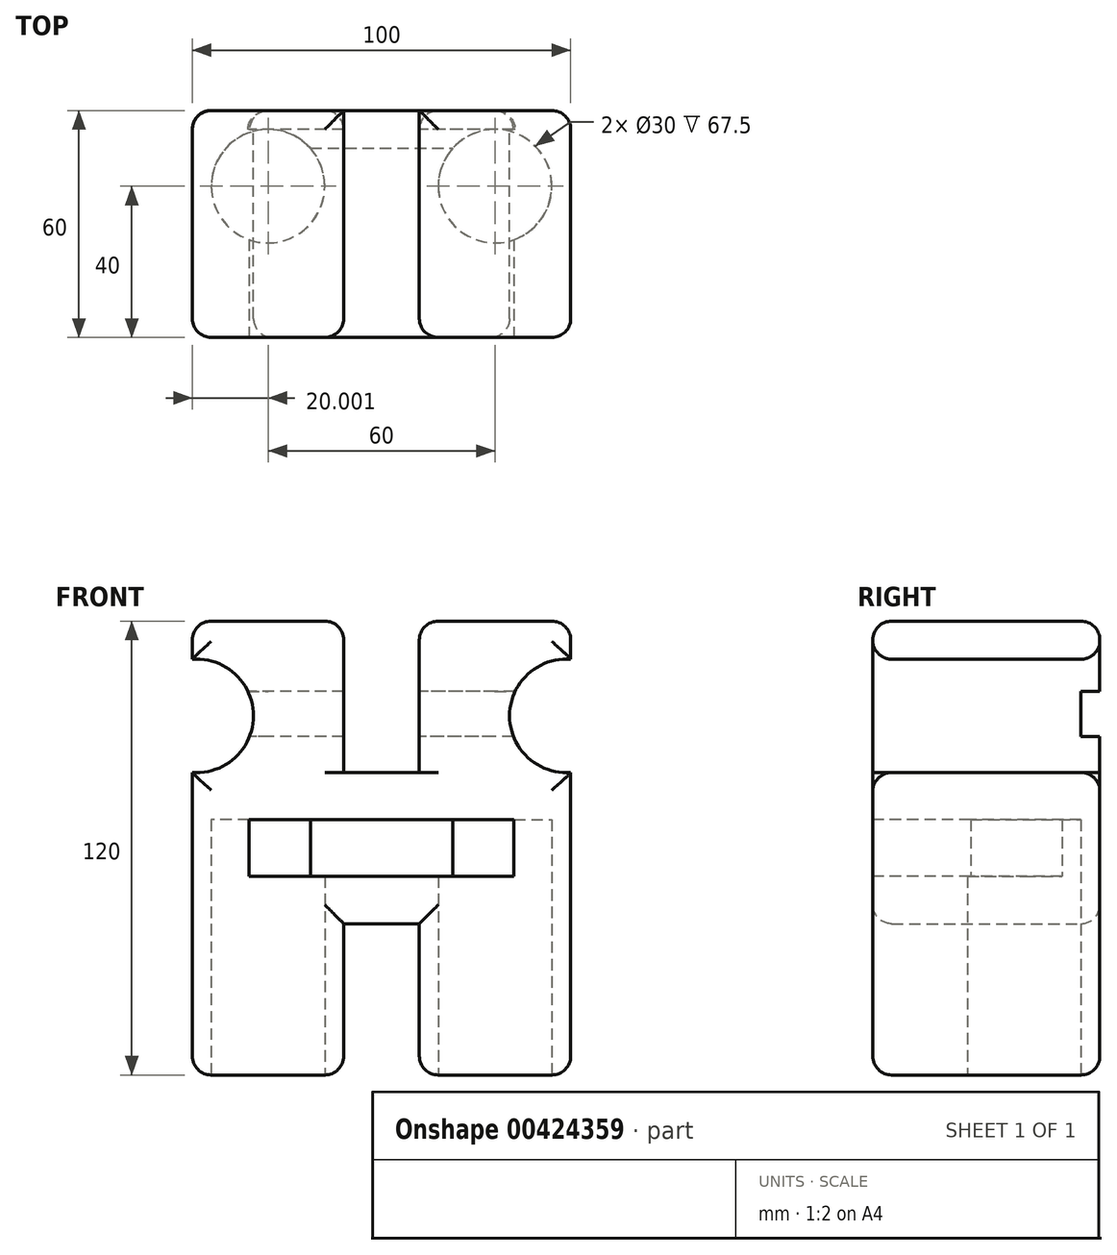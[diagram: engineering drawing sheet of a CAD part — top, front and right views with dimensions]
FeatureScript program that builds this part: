
annotation { "Feature Type Name" : "Feature", "Feature Type Description" : "" }
export const myFeature = defineFeature(function(context is Context, id is Id, definition is map)
    precondition{}
    {
        {
            var Q0;
            Q0=qCreatedBy(makeId("Front.planeOp"),FACE);
            var sketch = newSketch(context, id + "F0", { "sketchPlane" : qUnion([Q0])});
            skLineSegment(sketch, "E0.bottom", {"start": v(-48.04, 59.25) * mm, "end": v(-8.04, 59.25) * mm});
            skLineSegment(sketch, "E0.top", {"start": v(-48.04, -60.75) * mm, "end": v(-8.04, -60.75) * mm});
            skLineSegment(sketch, "E0.left", {"start": v(-48.04, 19.25) * mm, "end": v(-48.04, -60.75) * mm});
            skLineSegment(sketch, "E0.right", {"start": v(51.96, 19.25) * mm, "end": v(51.96, -60.75) * mm});
            skLineSegment(sketch, "E1", {"start": v(-8.04, 59.25) * mm, "end": v(-8.04, 19.25) * mm});
            skLineSegment(sketch, "E2", {"start": v(-8.04, 19.25) * mm, "end": v(11.96, 19.25) * mm});
            skLineSegment(sketch, "E3", {"start": v(11.96, 19.25) * mm, "end": v(11.96, 59.25) * mm});
            skLineSegment(sketch, "E4", {"start": v(11.96, -60.75) * mm, "end": v(11.96, -20.75) * mm});
            skLineSegment(sketch, "E5", {"start": v(11.96, -20.75) * mm, "end": v(-8.04, -20.75) * mm});
            skLineSegment(sketch, "E6", {"start": v(-8.04, -20.75) * mm, "end": v(-8.04, -60.75) * mm});
            skLineSegment(sketch, "E7.trimOffspring", {"start": v(11.96, -60.75) * mm, "end": v(51.96, -60.75) * mm});
            skLineSegment(sketch, "E8.trimOffspring", {"start": v(11.96, 59.25) * mm, "end": v(51.96, 59.25) * mm});
            skLineSegment(sketch, "E9", {"start": v(11.96, 19.25) * mm, "end": v(-8.04, 19.25) * mm});
            skLineSegment(sketch, "E10", {"start": v(-48.04, 59.25) * mm, "end": v(-48.04, 49.16) * mm});
            skLineSegment(sketch, "E11", {"start": v(51.96, 59.25) * mm, "end": v(51.96, 49.16) * mm});
            skArc(sketch, "E12", {"start": v(-48.04, 19.25) * mm, "mid": v(-31.88, 34.2) * mm, "end": v(-48.04, 49.16) * mm});
            skArc(sketch, "E13", {"start": v(51.96, 49.16) * mm, "mid": v(35.8, 34.2) * mm, "end": v(51.96, 19.25) * mm});
            skSolve(sketch);
        }
        {
            var Q0;
            Q0=makeQuery(id+"F0.imprint","IMPRINT",FACE,{"disambiguationData":[TD([[makeQuery(id+"F0.imprint","IMPRINT",EDGE,{"derivedFrom":sQuery(id+"F0.wireOp",EDGE,"E0.bottom")}),-1.0]])]});
            extrude(context, id + "F1", {"entities" : qUnion([Q0]), "depth" : 60 * mm});
        }
        {
            var Q0;
            Q0=makeQuery(id+"F1.opExtrude","CAP_FACE",FACE,{"disambiguationData":[OSD([sQuery(id+"F0.wireOp",EDGE,"E0.bottom"),sQuery(id+"F0.wireOp",EDGE,"E0.top"),sQuery(id+"F0.wireOp",EDGE,"E0.left"),sQuery(id+"F0.wireOp",EDGE,"E0.right"),sQuery(id+"F0.wireOp",EDGE,"E1"),sQuery(id+"F0.wireOp",EDGE,"E2"),sQuery(id+"F0.wireOp",EDGE,"E3"),sQuery(id+"F0.wireOp",EDGE,"E4"),sQuery(id+"F0.wireOp",EDGE,"E5"),sQuery(id+"F0.wireOp",EDGE,"E6"),sQuery(id+"F0.wireOp",EDGE,"E7.trimOffspring"),sQuery(id+"F0.wireOp",EDGE,"E8.trimOffspring")])],"isStart":false});
            var sketch = newSketch(context, id + "F2", { "sketchPlane" : qUnion([Q0])});
            skLineSegment(sketch, "E14.bottom", {"start": v(-33.04, 6.75) * mm, "end": v(36.96, 6.75) * mm});
            skLineSegment(sketch, "E14.top", {"start": v(-33.04, -8.25) * mm, "end": v(36.96, -8.25) * mm});
            skLineSegment(sketch, "E14.left", {"start": v(-33.04, 6.75) * mm, "end": v(-33.04, -8.25) * mm});
            skLineSegment(sketch, "E14.right", {"start": v(36.96, 6.75) * mm, "end": v(36.96, -8.25) * mm});
            skSolve(sketch);
        }
        {
            var Q0;
            Q0=makeQuery(id+"F2.imprint","IMPRINT",FACE,{"disambiguationData":[TD([[makeQuery(id+"F2.imprint","IMPRINT",EDGE,{"derivedFrom":sQuery(id+"F2.wireOp",EDGE,"E14.bottom")}),-1.0]])]});
            extrude(context, id + "F3", {"entities" : qUnion([Q0]), "operationType" : NewBodyOperationType.REMOVE, "oppositeDirection" : true, "depth" : 50 * mm});
        }
        {
            var Q0;
            Q0=makeQuery(id+"F1.opExtrude","SWEPT_FACE",FACE,{"disambiguationData":[OSD([sQuery(id+"F0.wireOp",EDGE,"E0.top")])]});
            var sketch = newSketch(context, id + "F4", { "sketchPlane" : qUnion([Q0])});
            skCircle(sketch, "E15", {"center": v(-28.04, 20) * mm, "radius": 15 * mm});
            skSolve(sketch);
        }
        {
            var Q0;
            Q0=makeQuery(id+"F1.opExtrude","SWEPT_FACE",FACE,{"disambiguationData":[OSD([sQuery(id+"F0.wireOp",EDGE,"E7.trimOffspring")])]});
            var sketch = newSketch(context, id + "F5", { "sketchPlane" : qUnion([Q0])});
            skCircle(sketch, "E16", {"center": v(31.96, 20) * mm, "radius": 15 * mm});
            skSolve(sketch);
        }
        {
            var Q0;
            Q0=makeQuery(id+"F4.imprint","IMPRINT",FACE,{"disambiguationData":[TD([[makeQuery(id+"F4.imprint","IMPRINT",EDGE,{"derivedFrom":sQuery(id+"F4.wireOp",EDGE,"E15")}),1.0]])]});
            var Q1;
            Q1=makeQuery(id+"F5.imprint","IMPRINT",FACE,{"disambiguationData":[TD([[makeQuery(id+"F5.imprint","IMPRINT",EDGE,{"derivedFrom":sQuery(id+"F5.wireOp",EDGE,"E16")}),1.0]])]});
            var Q2;
            Q2=sQuery(id+"F4.wireOp",EDGE,"E15");
            extrude(context, id + "F6", {"entities" : qUnion([Q0, Q1]), "operationType" : NewBodyOperationType.REMOVE, "surfaceEntities" : qUnion([Q2]), "oppositeDirection" : true, "depth" : 67.5 * mm});
        }
        {
            var Q0;
            Q0=makeQuery(id+"F0.imprint","IMPRINT",FACE,{"disambiguationData":[TD([[makeQuery(id+"F0.imprint","IMPRINT",EDGE,{"derivedFrom":sQuery(id+"F0.wireOp",EDGE,"E0.bottom")}),-1.0]])]});
            var sketch = newSketch(context, id + "F7", { "sketchPlane" : qUnion([Q0])});
            skLineSegment(sketch, "E17.bottom", {"start": v(38, 40.7) * mm, "end": v(-38.4, 40.7) * mm});
            skLineSegment(sketch, "E17.top", {"start": v(38, 28.7) * mm, "end": v(-38.4, 28.7) * mm});
            skLineSegment(sketch, "E17.left", {"start": v(38, 40.7) * mm, "end": v(38, 28.7) * mm});
            skLineSegment(sketch, "E17.right", {"start": v(-38.4, 40.7) * mm, "end": v(-38.4, 28.7) * mm});
            skSolve(sketch);
        }
        {
            var Q0;
            {var subQ0=sQuery(id+"F7.wireOp",EDGE,"E17.left");Q0=makeQuery(id+"F7.imprint","IMPRINT",FACE,{"disambiguationData":[TD([[makeQuery(id+"F7.imprint","IMPRINT",EDGE,{"derivedFrom":subQ0}),-1.0]])]});}
            var Q1;
            {var subQ0=sQuery(id+"F7.wireOp",EDGE,"E17.bottom");var subQ1=makeQuery(id+"F0.imprint","IMPRINT",EDGE,{"derivedFrom":sQuery(id+"F0.wireOp",EDGE,"E3")});var subQ2=makeQuery(id+"F7.imprint","INTERSECT",VERTEX,{"derivedFrom":[subQ1,subQ0]});Q1=makeQuery(id+"F7.imprint","IMPRINT",FACE,{"disambiguationData":[TD([[makeQuery(id+"F7.imprint","IMPRINT",EDGE,{"disambiguationData":[TD([[subQ2,-1.0]])],"derivedFrom":subQ0}),1.0]])]});}
            var Q2;
            {var subQ0=sQuery(id+"F7.wireOp",EDGE,"E17.bottom");var subQ1=makeQuery(id+"F0.imprint","IMPRINT",EDGE,{"derivedFrom":sQuery(id+"F0.wireOp",EDGE,"E1")});var subQ2=makeQuery(id+"F7.imprint","INTERSECT",VERTEX,{"derivedFrom":[subQ1,subQ0]});Q2=makeQuery(id+"F7.imprint","IMPRINT",FACE,{"disambiguationData":[TD([[makeQuery(id+"F7.imprint","IMPRINT",EDGE,{"disambiguationData":[TD([[subQ2,-1.0]])],"derivedFrom":subQ0}),1.0]])]});}
            var Q3;
            {var subQ0=sQuery(id+"F7.wireOp",EDGE,"E17.right");Q3=makeQuery(id+"F7.imprint","IMPRINT",FACE,{"disambiguationData":[TD([[makeQuery(id+"F7.imprint","IMPRINT",EDGE,{"derivedFrom":subQ0}),1.0]])]});}
            var Q4;
            {var subQ0=sQuery(id+"F7.wireOp",EDGE,"E17.bottom");var subQ1=makeQuery(id+"F0.imprint","IMPRINT",EDGE,{"derivedFrom":sQuery(id+"F0.wireOp",EDGE,"E13")});var subQ2=makeQuery(id+"F7.imprint","INTERSECT",VERTEX,{"derivedFrom":[subQ1,subQ0]});Q4=makeQuery(id+"F7.imprint","IMPRINT",FACE,{"disambiguationData":[TD([[makeQuery(id+"F7.imprint","IMPRINT",EDGE,{"disambiguationData":[TD([[subQ2,-1.0]])],"derivedFrom":subQ0}),1.0]])]});}
            extrude(context, id + "F8", {"entities" : qUnion([Q0, Q1, Q2, Q3, Q4]), "operationType" : NewBodyOperationType.REMOVE, "depth" : 5 * mm});
        }
        {
            var Q0;
            Q0=makeQuery(id+"F1.opExtrude","CAP_EDGE",EDGE,{"disambiguationData":[OSD([sQuery(id+"F0.wireOp",EDGE,"E12")])],"isStart":false});
            var Q1;
            Q1=makeQuery(id+"F1.opExtrude","CAP_EDGE",EDGE,{"disambiguationData":[OSD([sQuery(id+"F0.wireOp",EDGE,"E10")])],"isStart":false});
            var Q2;
            Q2=makeQuery(id+"F1.opExtrude","CAP_EDGE",EDGE,{"disambiguationData":[OSD([sQuery(id+"F0.wireOp",EDGE,"E0.bottom")])],"isStart":false});
            var Q3;
            Q3=makeQuery(id+"F1.opExtrude","CAP_EDGE",EDGE,{"disambiguationData":[OSD([sQuery(id+"F0.wireOp",EDGE,"E1")])],"isStart":false});
            var Q4;
            Q4=makeQuery(id+"F1.opExtrude","CAP_EDGE",EDGE,{"disambiguationData":[OSD([sQuery(id+"F0.wireOp",EDGE,"E9")])],"isStart":false});
            var Q5;
            Q5=makeQuery(id+"F1.opExtrude","CAP_EDGE",EDGE,{"disambiguationData":[OSD([sQuery(id+"F0.wireOp",EDGE,"E3")])],"isStart":false});
            var Q6;
            Q6=makeQuery(id+"F1.opExtrude","CAP_EDGE",EDGE,{"disambiguationData":[OSD([sQuery(id+"F0.wireOp",EDGE,"E8.trimOffspring")])],"isStart":false});
            var Q7;
            Q7=makeQuery(id+"F1.opExtrude","CAP_EDGE",EDGE,{"disambiguationData":[OSD([sQuery(id+"F0.wireOp",EDGE,"E11")])],"isStart":false});
            var Q8;
            Q8=makeQuery(id+"F1.opExtrude","CAP_EDGE",EDGE,{"disambiguationData":[OSD([sQuery(id+"F0.wireOp",EDGE,"E13")])],"isStart":false});
            var Q9;
            Q9=makeQuery(id+"F1.opExtrude","CAP_EDGE",EDGE,{"disambiguationData":[OSD([sQuery(id+"F0.wireOp",EDGE,"E0.right")])],"isStart":false});
            var Q10;
            Q10=makeQuery(id+"F1.opExtrude","CAP_EDGE",EDGE,{"disambiguationData":[OSD([sQuery(id+"F0.wireOp",EDGE,"E0.left")])],"isStart":false});
            var Q11;
            Q11=makeQuery(id+"F1.opExtrude","CAP_EDGE",EDGE,{"disambiguationData":[OSD([sQuery(id+"F0.wireOp",EDGE,"E0.top")])],"isStart":false});
            var Q12;
            Q12=makeQuery(id+"F1.opExtrude","CAP_EDGE",EDGE,{"disambiguationData":[OSD([sQuery(id+"F0.wireOp",EDGE,"E7.trimOffspring")])],"isStart":false});
            var Q13;
            Q13=makeQuery(id+"F1.opExtrude","CAP_EDGE",EDGE,{"disambiguationData":[OSD([sQuery(id+"F0.wireOp",EDGE,"E4")])],"isStart":false});
            var Q14;
            Q14=makeQuery(id+"F1.opExtrude","CAP_EDGE",EDGE,{"disambiguationData":[OSD([sQuery(id+"F0.wireOp",EDGE,"E6")])],"isStart":false});
            var Q15;
            Q15=makeQuery(id+"F1.opExtrude","CAP_EDGE",EDGE,{"disambiguationData":[OSD([sQuery(id+"F0.wireOp",EDGE,"E5")])],"isStart":false});
            var Q16;
            Q16=makeQuery(id+"F3.boolean.opBoolean","COPY",EDGE,{"derivedFrom":makeQuery(id+"F3.opExtrude","CAP_EDGE",EDGE,{"disambiguationData":[OSD([sQuery(id+"F2.wireOp",EDGE,"E14.top")])],"isStart":true})});
            var Q17;
            Q17=makeQuery(id+"F3.boolean.opBoolean","COPY",EDGE,{"derivedFrom":makeQuery(id+"F3.opExtrude","CAP_EDGE",EDGE,{"disambiguationData":[OSD([sQuery(id+"F2.wireOp",EDGE,"E14.bottom")])],"isStart":true})});
            var Q18;
            Q18=makeQuery(id+"F1.opExtrude","SWEPT_EDGE",EDGE,{"disambiguationData":[OSD([sQuery(id+"F0.wireOp",EDGE,"E8.trimOffspring"),sQuery(id+"F0.wireOp",EDGE,"E11")])]});
            var Q19;
            Q19=makeQuery(id+"F1.opExtrude","SWEPT_EDGE",EDGE,{"disambiguationData":[OSD([sQuery(id+"F0.wireOp",EDGE,"E3"),sQuery(id+"F0.wireOp",EDGE,"E8.trimOffspring")])]});
            var Q20;
            Q20=makeQuery(id+"F1.opExtrude","SWEPT_EDGE",EDGE,{"disambiguationData":[OSD([sQuery(id+"F0.wireOp",EDGE,"E0.bottom"),sQuery(id+"F0.wireOp",EDGE,"E1")])]});
            var Q21;
            Q21=makeQuery(id+"F1.opExtrude","SWEPT_EDGE",EDGE,{"disambiguationData":[OSD([sQuery(id+"F0.wireOp",EDGE,"E0.bottom"),sQuery(id+"F0.wireOp",EDGE,"E10")])]});
            var Q22;
            Q22=makeQuery(id+"F1.opExtrude","CAP_EDGE",EDGE,{"disambiguationData":[OSD([sQuery(id+"F0.wireOp",EDGE,"E8.trimOffspring")])],"isStart":true});
            var Q23;
            Q23=makeQuery(id+"F1.opExtrude","CAP_EDGE",EDGE,{"disambiguationData":[OSD([sQuery(id+"F0.wireOp",EDGE,"E0.bottom")])],"isStart":true});
            var Q24;
            {var subQ0=sQuery(id+"F0.wireOp",EDGE,"E13");var subQ1=sQuery(id+"F0.wireOp",EDGE,"E11");Q24=makeQuery(id+"F8.boolean.opBoolean","SPLIT",EDGE,{"disambiguationData":[TD([makeQuery(id+"F1.opExtrude","SWEPT_FACE",FACE,{"disambiguationData":[OSD([subQ1])]})])],"derivedFrom":makeQuery(id+"F1.opExtrude","CAP_EDGE",EDGE,{"disambiguationData":[OSD([subQ0])],"isStart":true})});}
            var Q25;
            {var subQ0=sQuery(id+"F0.wireOp",EDGE,"E13");var subQ1=sQuery(id+"F0.wireOp",EDGE,"E0.right");Q25=makeQuery(id+"F8.boolean.opBoolean","SPLIT",EDGE,{"disambiguationData":[TD([makeQuery(id+"F1.opExtrude","SWEPT_FACE",FACE,{"disambiguationData":[OSD([subQ1])]})])],"derivedFrom":makeQuery(id+"F1.opExtrude","CAP_EDGE",EDGE,{"disambiguationData":[OSD([subQ0])],"isStart":true})});}
            var Q26;
            {var subQ0=sQuery(id+"F0.wireOp",EDGE,"E12");var subQ1=sQuery(id+"F0.wireOp",EDGE,"E0.left");Q26=makeQuery(id+"F8.boolean.opBoolean","SPLIT",EDGE,{"disambiguationData":[TD([makeQuery(id+"F1.opExtrude","SWEPT_FACE",FACE,{"disambiguationData":[OSD([subQ1])]})])],"derivedFrom":makeQuery(id+"F1.opExtrude","CAP_EDGE",EDGE,{"disambiguationData":[OSD([subQ0])],"isStart":true})});}
            var Q27;
            {var subQ0=sQuery(id+"F0.wireOp",EDGE,"E12");var subQ1=sQuery(id+"F0.wireOp",EDGE,"E10");Q27=makeQuery(id+"F8.boolean.opBoolean","SPLIT",EDGE,{"disambiguationData":[TD([makeQuery(id+"F1.opExtrude","SWEPT_FACE",FACE,{"disambiguationData":[OSD([subQ1])]})])],"derivedFrom":makeQuery(id+"F1.opExtrude","CAP_EDGE",EDGE,{"disambiguationData":[OSD([subQ0])],"isStart":true})});}
            var Q28;
            Q28=makeQuery(id+"F1.opExtrude","CAP_EDGE",EDGE,{"disambiguationData":[OSD([sQuery(id+"F0.wireOp",EDGE,"E11")])],"isStart":true});
            var Q29;
            Q29=makeQuery(id+"F1.opExtrude","CAP_EDGE",EDGE,{"disambiguationData":[OSD([sQuery(id+"F0.wireOp",EDGE,"E10")])],"isStart":true});
            var Q30;
            Q30=makeQuery(id+"F1.opExtrude","CAP_EDGE",EDGE,{"disambiguationData":[OSD([sQuery(id+"F0.wireOp",EDGE,"E0.left")])],"isStart":true});
            var Q31;
            Q31=makeQuery(id+"F1.opExtrude","CAP_EDGE",EDGE,{"disambiguationData":[OSD([sQuery(id+"F0.wireOp",EDGE,"E0.right")])],"isStart":true});
            var Q32;
            Q32=makeQuery(id+"F1.opExtrude","CAP_EDGE",EDGE,{"disambiguationData":[OSD([sQuery(id+"F0.wireOp",EDGE,"E0.top")])],"isStart":true});
            var Q33;
            Q33=makeQuery(id+"F1.opExtrude","CAP_EDGE",EDGE,{"disambiguationData":[OSD([sQuery(id+"F0.wireOp",EDGE,"E7.trimOffspring")])],"isStart":true});
            var Q34;
            Q34=makeQuery(id+"F1.opExtrude","CAP_EDGE",EDGE,{"disambiguationData":[OSD([sQuery(id+"F0.wireOp",EDGE,"E6")])],"isStart":true});
            var Q35;
            Q35=makeQuery(id+"F1.opExtrude","CAP_EDGE",EDGE,{"disambiguationData":[OSD([sQuery(id+"F0.wireOp",EDGE,"E4")])],"isStart":true});
            var Q36;
            Q36=makeQuery(id+"F1.opExtrude","CAP_EDGE",EDGE,{"disambiguationData":[OSD([sQuery(id+"F0.wireOp",EDGE,"E5")])],"isStart":true});
            var Q37;
            Q37=makeQuery(id+"F1.opExtrude","SWEPT_EDGE",EDGE,{"disambiguationData":[OSD([sQuery(id+"F0.wireOp",EDGE,"E4"),sQuery(id+"F0.wireOp",EDGE,"E7.trimOffspring")])]});
            var Q38;
            Q38=makeQuery(id+"F1.opExtrude","SWEPT_EDGE",EDGE,{"disambiguationData":[OSD([sQuery(id+"F0.wireOp",EDGE,"E0.top"),sQuery(id+"F0.wireOp",EDGE,"E6")])]});
            var Q39;
            Q39=makeQuery(id+"F1.opExtrude","SWEPT_EDGE",EDGE,{"disambiguationData":[OSD([sQuery(id+"F0.wireOp",EDGE,"E0.top"),sQuery(id+"F0.wireOp",EDGE,"E0.left")])]});
            var Q40;
            Q40=makeQuery(id+"F1.opExtrude","SWEPT_EDGE",EDGE,{"disambiguationData":[OSD([sQuery(id+"F0.wireOp",EDGE,"E0.right"),sQuery(id+"F0.wireOp",EDGE,"E7.trimOffspring")])]});
            fillet(context, id + "F9", {"entities" : qUnion([Q0, Q1, Q2, Q3, Q4, Q5, Q6, Q7, Q8, Q9, Q10, Q11, Q12, Q13, Q14, Q15, Q16, Q17, Q18, Q19, Q20, Q21, Q22, Q23, Q24, Q25, Q26, Q27, Q28, Q29, Q30, Q31, Q32, Q33, Q34, Q35, Q36, Q37, Q38, Q39, Q40]), "radius" : 5 * mm, "tangentPropagation" : true, "allowEdgeOverflow" : false});
        }
    });
